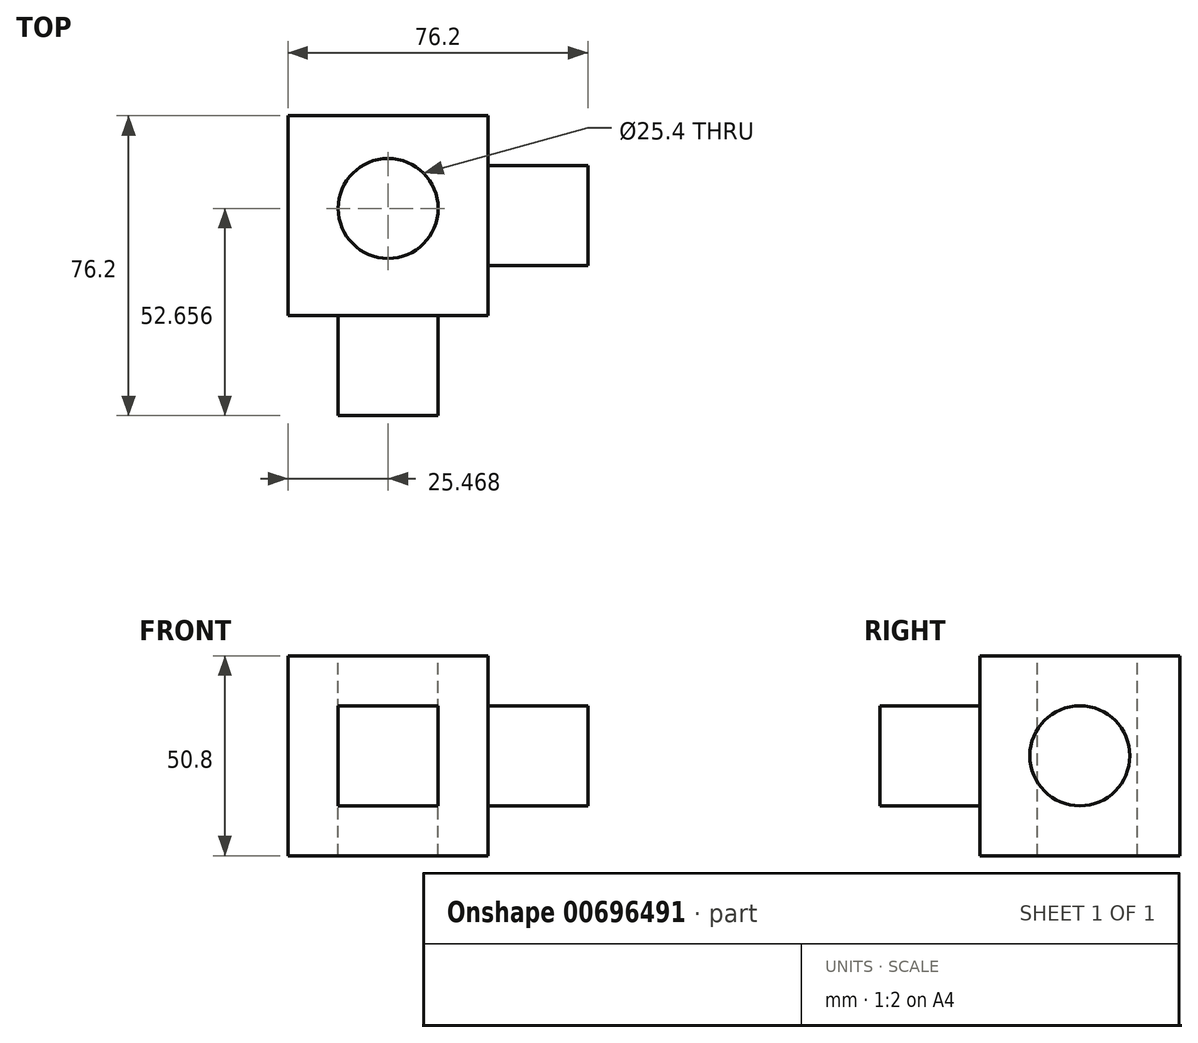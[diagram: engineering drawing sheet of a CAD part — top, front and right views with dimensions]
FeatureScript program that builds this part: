
annotation { "Feature Type Name" : "Feature", "Feature Type Description" : "" }
export const myFeature = defineFeature(function(context is Context, id is Id, definition is map)
    precondition{}
    {
        {
            var Q0;
            Q0=qCreatedBy(makeId("Front.planeOp"),FACE);
            var sketch = newSketch(context, id + "F0", { "sketchPlane" : qUnion([Q0])});
            skLineSegment(sketch, "E0.bottom", {"start": v(0, 0) * mm, "end": v(-50.8, 0) * mm});
            skLineSegment(sketch, "E0.top", {"start": v(0, 50.8) * mm, "end": v(-50.8, 50.8) * mm});
            skLineSegment(sketch, "E0.left", {"start": v(0, 0) * mm, "end": v(0, 50.8) * mm});
            skLineSegment(sketch, "E0.right", {"start": v(-50.8, 0) * mm, "end": v(-50.8, 50.8) * mm});
            skSolve(sketch);
        }
        {
            var Q0;
            Q0=makeQuery(id+"F0.imprint","IMPRINT",FACE,{"disambiguationData":[TD([[makeQuery(id+"F0.imprint","IMPRINT",EDGE,{"derivedFrom":sQuery(id+"F0.wireOp",EDGE,"E0.bottom")}),-1.0]])]});
            extrude(context, id + "F1", {"entities" : qUnion([Q0]), "depth" : 50.8 * mm, "offsetDistance" : 25.4 * mm});
        }
        {
            var Q0;
            Q0=makeQuery(id+"F1.opExtrude","SWEPT_FACE",FACE,{"disambiguationData":[OSD([sQuery(id+"F0.wireOp",EDGE,"E0.top")])]});
            var sketch = newSketch(context, id + "F2", { "sketchPlane" : qUnion([Q0])});
            skCircle(sketch, "E1", {"center": v(-25.33, -23.54) * mm, "radius": 12.7 * mm});
            skSolve(sketch);
        }
        {
            var Q0;
            Q0=makeQuery(id+"F2.imprint","IMPRINT",FACE,{"disambiguationData":[TD([[makeQuery(id+"F2.imprint","IMPRINT",EDGE,{"derivedFrom":sQuery(id+"F2.wireOp",EDGE,"E1")}),1.0]])]});
            extrude(context, id + "F3", {"entities" : qUnion([Q0]), "operationType" : NewBodyOperationType.REMOVE, "oppositeDirection" : true, "depth" : 50.8 * mm, "offsetDistance" : 25.4 * mm});
        }
        {
            var Q0;
            Q0=makeQuery(id+"F1.opExtrude","CAP_FACE",FACE,{"disambiguationData":[OSD([sQuery(id+"F0.wireOp",EDGE,"E0.bottom"),sQuery(id+"F0.wireOp",EDGE,"E0.top"),sQuery(id+"F0.wireOp",EDGE,"E0.left"),sQuery(id+"F0.wireOp",EDGE,"E0.right")])],"isStart":false});
            var sketch = newSketch(context, id + "F4", { "sketchPlane" : qUnion([Q0])});
            skLineSegment(sketch, "E2.bottom", {"start": v(-38.1, 38.1) * mm, "end": v(-12.7, 38.1) * mm});
            skLineSegment(sketch, "E2.top", {"start": v(-38.1, 12.7) * mm, "end": v(-12.7, 12.7) * mm});
            skLineSegment(sketch, "E2.left", {"start": v(-38.1, 38.1) * mm, "end": v(-38.1, 12.7) * mm});
            skLineSegment(sketch, "E2.right", {"start": v(-12.7, 38.1) * mm, "end": v(-12.7, 12.7) * mm});
            skSolve(sketch);
        }
        {
            var Q0;
            Q0=makeQuery(id+"F4.imprint","IMPRINT",FACE,{"disambiguationData":[TD([[makeQuery(id+"F4.imprint","IMPRINT",EDGE,{"derivedFrom":sQuery(id+"F4.wireOp",EDGE,"E2.bottom")}),-1.0]])]});
            extrude(context, id + "F5", {"entities" : qUnion([Q0]), "operationType" : NewBodyOperationType.ADD, "depth" : 25.4 * mm, "offsetDistance" : 25.4 * mm});
        }
        {
            var Q0;
            Q0=makeQuery(id+"F1.opExtrude","SWEPT_FACE",FACE,{"disambiguationData":[OSD([sQuery(id+"F0.wireOp",EDGE,"E0.left")])]});
            var sketch = newSketch(context, id + "F6", { "sketchPlane" : qUnion([Q0])});
            skCircle(sketch, "E3", {"center": v(-25.4, 25.4) * mm, "radius": 12.7 * mm});
            skSolve(sketch);
        }
        {
            var Q0;
            Q0=makeQuery(id+"F6.imprint","IMPRINT",FACE,{"disambiguationData":[TD([[makeQuery(id+"F6.imprint","IMPRINT",EDGE,{"derivedFrom":sQuery(id+"F6.wireOp",EDGE,"E3")}),1.0]])]});
            extrude(context, id + "F7", {"entities" : qUnion([Q0]), "operationType" : NewBodyOperationType.ADD, "depth" : 25.4 * mm, "offsetDistance" : 25.4 * mm});
        }
    });
